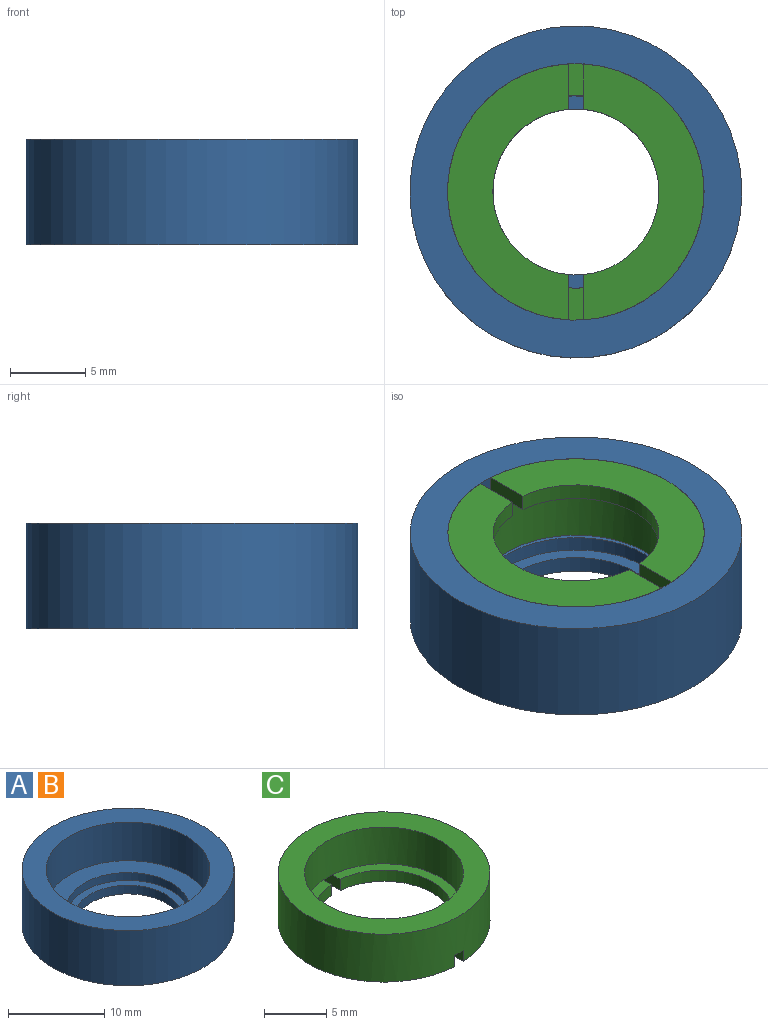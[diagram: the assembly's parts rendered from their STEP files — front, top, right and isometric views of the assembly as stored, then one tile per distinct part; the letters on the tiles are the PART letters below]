
ASSEMBLY  parts=3 mates=1
PART A: 8 faces, bbox 22x22x7 mm
  f0: plane 17x17mm, normal (0,0,1), area 99.3mm2, adj f5,f6
  f1: plane 12.75x12.75mm, normal (0,0,1), area 32.6mm2, adj f2,f5
  f2: cylinder r=5.5mm len=11mm, axis (0,0,-1), area 38mm2, adj f1,f4
  f3: cylinder r=11mm len=22mm, axis (0,0,-1), area 483.8mm2, adj f4,f7
  f4: plane 22x22mm, normal (0,0,-1), area 285.1mm2, adj f2,f3
  f5: cylinder r=6.38mm len=12.75mm, axis (0,0,-1), area 40.1mm2, adj f0,f1
  f6: cylinder r=8.5mm len=17mm, axis (0,0,-1), area 261.7mm2, adj f0,f7
  f7: plane 22x22mm, normal (0,0,1), area 153.2mm2, adj f3,f6
PART B: same geometry as A
PART C: 15 faces, bbox 17x17x4.7 mm
  f0: plane 12.71x5.88mm, normal (0,0,1), area 15.4mm2, adj f2,f7,f10,f13
  f1: cylinder r=5.5mm len=10.95mm, axis (0,0,-1), area 17.9mm2, adj f3,f5,f11,f14
  f2: cylinder r=5.5mm len=10.95mm, axis (0,0,-1), area 17.9mm2, adj f0,f4,f10,f13
  f3: plane 16.97x8mm, normal (0,0,-1), area 63mm2, adj f1,f6,f11,f14
  f4: plane 16.97x8mm, normal (0,0,-1), area 63mm2, adj f2,f6,f10,f13
  f5: plane 12.71x5.88mm, normal (0,0,1), area 15.4mm2, adj f1,f7,f11,f14
  f6: cylinder r=8.5mm len=17mm, axis (0,0,-1), area 248.8mm2, adj f3,f4,f8,f9,f10,f11,f12,f13
  f7: cylinder r=6.38mm len=12.75mm, axis (0,0,-1), area 144.2mm2, adj f0,f5,f8,f9,f12
  f8: plane 17x17mm, normal (0,0,1), area 99.3mm2, adj f6,f7
  f9: plane 2.14x1mm, normal (0,0,-1), area 2.1mm2, adj f6,f7,f10,f11
  f10: plane 3.01x1.1mm, normal (-1,0,0), area 3.3mm2, adj f0,f2,f4,f6,f9
  f11: plane 3.01x1.1mm, normal (1,0,0), area 3.3mm2, adj f1,f3,f5,f6,f9
  f12: plane 2.14x1mm, normal (0,0,-1), area 2.1mm2, adj f6,f7,f13,f14
  f13: plane 3.01x1.1mm, normal (-1,0,0), area 3.3mm2, adj f0,f2,f4,f6,f12
  f14: plane 3.01x1.1mm, normal (1,0,0), area 3.3mm2, adj f1,f3,f5,f6,f12
PLACE A t=(-1.26,1.48,-0.19)mm
PLACE B t=(-1.26,1.48,-0.19)mm
PLACE C rot(axis=(0,1,0),180deg) t=(30.88,1.48,6.81)mm
MATE planar C.f1 <-> A.f3  axis (0,0,1) through (-1.26,1.48,6.81)mm
